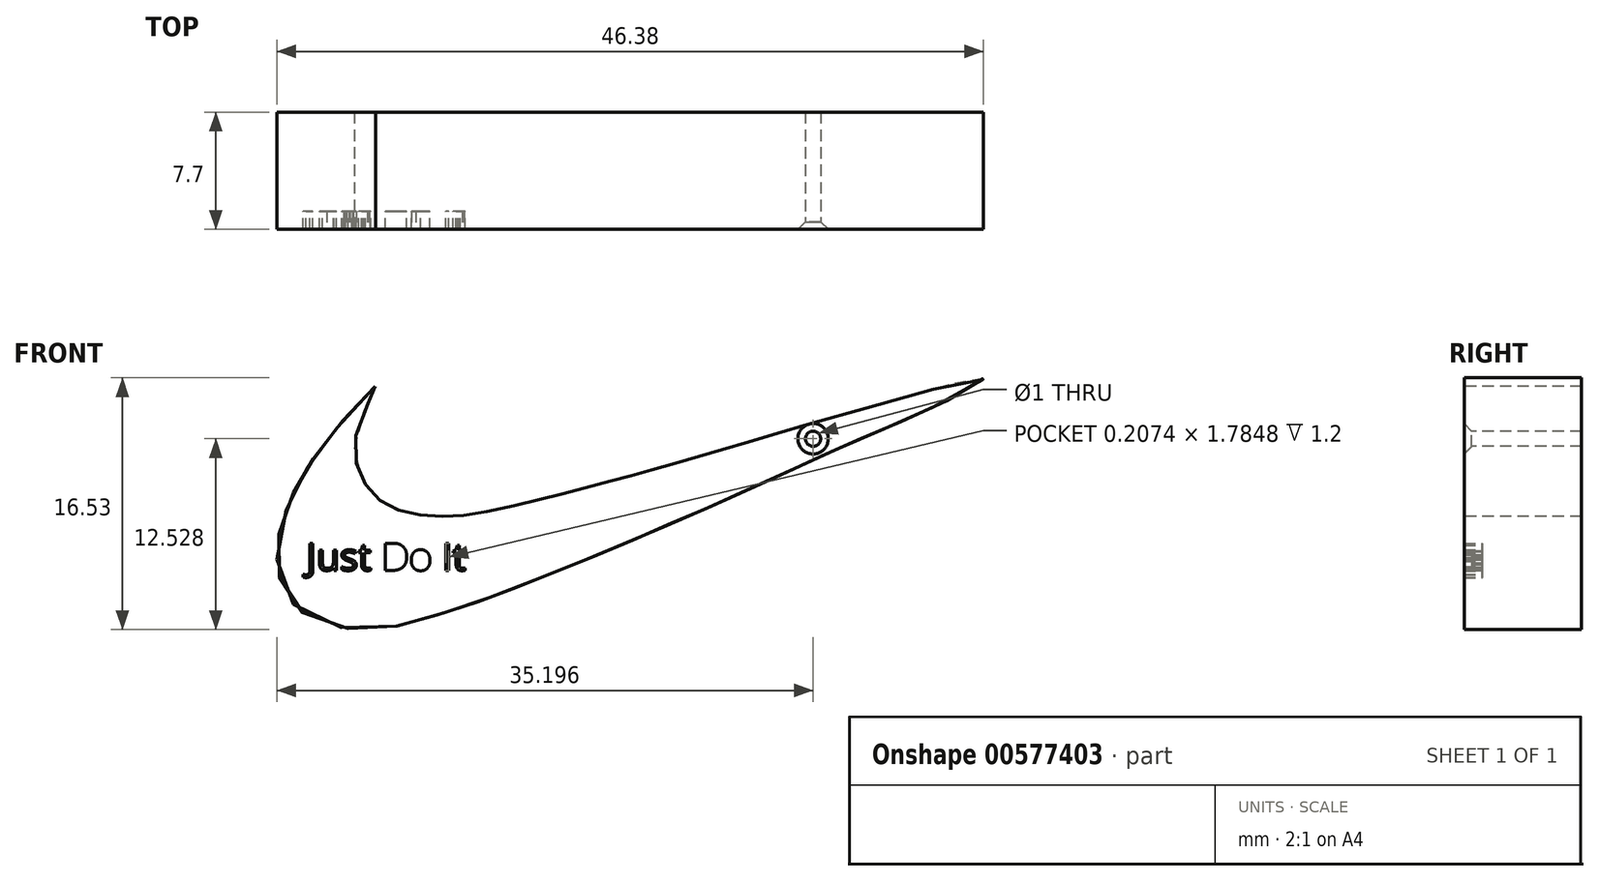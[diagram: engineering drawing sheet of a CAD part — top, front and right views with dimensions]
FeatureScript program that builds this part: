
annotation { "Feature Type Name" : "Feature", "Feature Type Description" : "" }
export const myFeature = defineFeature(function(context is Context, id is Id, definition is map)
    precondition{}
    {
        {
            var Q0;
            Q0=qCreatedBy(makeId("Front.planeOp"),FACE);
            var sketch = newSketch(context, id + "F0", { "sketchPlane" : qUnion([Q0])});
            skFitSpline(sketch, "E0", {"points": [v(-46.77, 38.6) * mm, v(-49.47, 35.68) * mm, v(-51.17, 33.36) * mm, v(-52.4, 31.05) * mm, v(-53.21, 28.05) * mm, v(-52.75, 25.22) * mm, v(-50.6, 23.19) * mm, v(-46.57, 22.67) * mm, v(-43.7, 23.3) * mm, v(-40.92, 24.16) * mm, v(-38.34, 25.09) * mm, v(-35.58, 26.17) * mm, v(-32.72, 27.33) * mm, v(-30.5, 28.24) * mm, v(-28.01, 29.32) * mm, v(-25.64, 30.33) * mm, v(-23.75, 31.18) * mm, v(-21.45, 32.21) * mm, v(-18.28, 33.67) * mm, v(-16.2, 34.6) * mm, v(-13.01, 35.97) * mm, v(-9.7, 37.46) * mm, v(-6.87, 39.13) * mm, v(-11.19, 38.12) * mm, v(-15.96, 36.8) * mm, v(-19.98, 35.64) * mm, v(-23.83, 34.5) * mm, v(-26.45, 33.75) * mm, v(-29.13, 32.98) * mm, v(-31.05, 32.46) * mm, v(-34, 31.67) * mm, v(-36.31, 31.1) * mm, v(-39.68, 30.34) * mm, v(-41.99, 30.07) * mm, v(-44.26, 30.24) * mm, v(-46.26, 30.96) * mm, v(-47.63, 32.56) * mm, v(-47.98, 35.73) * mm, v(-46.77, 38.6) * mm]});
            skSolve(sketch);
        }
        {
            var Q0;
            Q0 = qSketchRegion(id + "F0", true);
            extrude(context, id + "F1", {"entities" : qUnion([Q0]), "depth" : 6.5 * mm, "offsetDistance" : 25 * mm});
        }
        {
            var Q0;
            Q0=makeQuery(id+"F1.opExtrude","CAP_FACE",FACE,{"disambiguationData":[OSD([sQuery(id+"F0.wireOp",EDGE,"E0")])],"isStart":false});
            var sketch = newSketch(context, id + "F2", { "sketchPlane" : qUnion([Q0])});
            skText(sketch, "E1", { "text": "Just Do It", "fontName": "OpenSans-Regular.ttf"});
            const initialGuessF2  = {"E1": [-0.0513, 0.02652, 1, 0, 0.0018]};
            skSetInitialGuess(sketch, initialGuessF2);
            skSolve(sketch);
        }
        {
            var Q0;
            Q0=makeQuery(id+"F2.imprint","IMPRINT",FACE,{"disambiguationData":[TD([[makeQuery(id+"F2.imprint","IMPRINT",EDGE,{"derivedFrom":sQuery(id+"F2.wireOp",EDGE,"E1.sketch_text.stroke-0")}),1.0]])]});
            extrude(context, id + "F3", {"entities" : qUnion([Q0]), "operationType" : NewBodyOperationType.ADD, "depth" : 1.2 * mm, "offsetDistance" : 25 * mm});
        }
        {
            var Q0;
            Q0=makeQuery(id+"F3.opExtrude","CAP_FACE",FACE,{"disambiguationData":[OSD([sQuery(id+"F0.wireOp",EDGE,"E0"),sQuery(id+"F2.wireOp",EDGE,"E1.sketch_text.stroke-0"),sQuery(id+"F2.wireOp",EDGE,"E1.sketch_text.stroke-1"),sQuery(id+"F2.wireOp",EDGE,"E1.sketch_text.stroke-2"),sQuery(id+"F2.wireOp",EDGE,"E1.sketch_text.stroke-3"),sQuery(id+"F2.wireOp",EDGE,"E1.sketch_text.stroke-4"),sQuery(id+"F2.wireOp",EDGE,"E1.sketch_text.stroke-5"),sQuery(id+"F2.wireOp",EDGE,"E1.sketch_text.stroke-6"),sQuery(id+"F2.wireOp",EDGE,"E1.sketch_text.stroke-7"),sQuery(id+"F2.wireOp",EDGE,"E1.sketch_text.stroke-8"),sQuery(id+"F2.wireOp",EDGE,"E1.sketch_text.stroke-9"),sQuery(id+"F2.wireOp",EDGE,"E1.sketch_text.stroke-10"),sQuery(id+"F2.wireOp",EDGE,"E1.sketch_text.stroke-11"),sQuery(id+"F2.wireOp",EDGE,"E1.sketch_text.stroke-12"),sQuery(id+"F2.wireOp",EDGE,"E1.sketch_text.stroke-13"),sQuery(id+"F2.wireOp",EDGE,"E1.sketch_text.stroke-14"),sQuery(id+"F2.wireOp",EDGE,"E1.sketch_text.stroke-15"),sQuery(id+"F2.wireOp",EDGE,"E1.sketch_text.stroke-16"),sQuery(id+"F2.wireOp",EDGE,"E1.sketch_text.stroke-17"),sQuery(id+"F2.wireOp",EDGE,"E1.sketch_text.stroke-18"),sQuery(id+"F2.wireOp",EDGE,"E1.sketch_text.stroke-19"),sQuery(id+"F2.wireOp",EDGE,"E1.sketch_text.stroke-20"),sQuery(id+"F2.wireOp",EDGE,"E1.sketch_text.stroke-21"),sQuery(id+"F2.wireOp",EDGE,"E1.sketch_text.stroke-22"),sQuery(id+"F2.wireOp",EDGE,"E1.sketch_text.stroke-23"),sQuery(id+"F2.wireOp",EDGE,"E1.sketch_text.stroke-24"),sQuery(id+"F2.wireOp",EDGE,"E1.sketch_text.stroke-25"),sQuery(id+"F2.wireOp",EDGE,"E1.sketch_text.stroke-26"),sQuery(id+"F2.wireOp",EDGE,"E1.sketch_text.stroke-27"),sQuery(id+"F2.wireOp",EDGE,"E1.sketch_text.stroke-28"),sQuery(id+"F2.wireOp",EDGE,"E1.sketch_text.stroke-29"),sQuery(id+"F2.wireOp",EDGE,"E1.sketch_text.stroke-30"),sQuery(id+"F2.wireOp",EDGE,"E1.sketch_text.stroke-31"),sQuery(id+"F2.wireOp",EDGE,"E1.sketch_text.stroke-32"),sQuery(id+"F2.wireOp",EDGE,"E1.sketch_text.stroke-33"),sQuery(id+"F2.wireOp",EDGE,"E1.sketch_text.stroke-34"),sQuery(id+"F2.wireOp",EDGE,"E1.sketch_text.stroke-35"),sQuery(id+"F2.wireOp",EDGE,"E1.sketch_text.stroke-36"),sQuery(id+"F2.wireOp",EDGE,"E1.sketch_text.stroke-37"),sQuery(id+"F2.wireOp",EDGE,"E1.sketch_text.stroke-38"),sQuery(id+"F2.wireOp",EDGE,"E1.sketch_text.stroke-39"),sQuery(id+"F2.wireOp",EDGE,"E1.sketch_text.stroke-40"),sQuery(id+"F2.wireOp",EDGE,"E1.sketch_text.stroke-41"),sQuery(id+"F2.wireOp",EDGE,"E1.sketch_text.stroke-42"),sQuery(id+"F2.wireOp",EDGE,"E1.sketch_text.stroke-43"),sQuery(id+"F2.wireOp",EDGE,"E1.sketch_text.stroke-44"),sQuery(id+"F2.wireOp",EDGE,"E1.sketch_text.stroke-45"),sQuery(id+"F2.wireOp",EDGE,"E1.sketch_text.stroke-46"),sQuery(id+"F2.wireOp",EDGE,"E1.sketch_text.stroke-47"),sQuery(id+"F2.wireOp",EDGE,"E1.sketch_text.stroke-48"),sQuery(id+"F2.wireOp",EDGE,"E1.sketch_text.stroke-49"),sQuery(id+"F2.wireOp",EDGE,"E1.sketch_text.stroke-50"),sQuery(id+"F2.wireOp",EDGE,"E1.sketch_text.stroke-51"),sQuery(id+"F2.wireOp",EDGE,"E1.sketch_text.stroke-52"),sQuery(id+"F2.wireOp",EDGE,"E1.sketch_text.stroke-53"),sQuery(id+"F2.wireOp",EDGE,"E1.sketch_text.stroke-54"),sQuery(id+"F2.wireOp",EDGE,"E1.sketch_text.stroke-55"),sQuery(id+"F2.wireOp",EDGE,"E1.sketch_text.stroke-56"),sQuery(id+"F2.wireOp",EDGE,"E1.sketch_text.stroke-57"),sQuery(id+"F2.wireOp",EDGE,"E1.sketch_text.stroke-58"),sQuery(id+"F2.wireOp",EDGE,"E1.sketch_text.stroke-59"),sQuery(id+"F2.wireOp",EDGE,"E1.sketch_text.stroke-60"),sQuery(id+"F2.wireOp",EDGE,"E1.sketch_text.stroke-61"),sQuery(id+"F2.wireOp",EDGE,"E1.sketch_text.stroke-62"),sQuery(id+"F2.wireOp",EDGE,"E1.sketch_text.stroke-63"),sQuery(id+"F2.wireOp",EDGE,"E1.sketch_text.stroke-64"),sQuery(id+"F2.wireOp",EDGE,"E1.sketch_text.stroke-65"),sQuery(id+"F2.wireOp",EDGE,"E1.sketch_text.stroke-66"),sQuery(id+"F2.wireOp",EDGE,"E1.sketch_text.stroke-67"),sQuery(id+"F2.wireOp",EDGE,"E1.sketch_text.stroke-68"),sQuery(id+"F2.wireOp",EDGE,"E1.sketch_text.stroke-69"),sQuery(id+"F2.wireOp",EDGE,"E1.sketch_text.stroke-70"),sQuery(id+"F2.wireOp",EDGE,"E1.sketch_text.stroke-71"),sQuery(id+"F2.wireOp",EDGE,"E1.sketch_text.stroke-72"),sQuery(id+"F2.wireOp",EDGE,"E1.sketch_text.stroke-73"),sQuery(id+"F2.wireOp",EDGE,"E1.sketch_text.stroke-74"),sQuery(id+"F2.wireOp",EDGE,"E1.sketch_text.stroke-75"),sQuery(id+"F2.wireOp",EDGE,"E1.sketch_text.stroke-76"),sQuery(id+"F2.wireOp",EDGE,"E1.sketch_text.stroke-77"),sQuery(id+"F2.wireOp",EDGE,"E1.sketch_text.stroke-85"),sQuery(id+"F2.wireOp",EDGE,"E1.sketch_text.stroke-86"),sQuery(id+"F2.wireOp",EDGE,"E1.sketch_text.stroke-87"),sQuery(id+"F2.wireOp",EDGE,"E1.sketch_text.stroke-88"),sQuery(id+"F2.wireOp",EDGE,"E1.sketch_text.stroke-89"),sQuery(id+"F2.wireOp",EDGE,"E1.sketch_text.stroke-90"),sQuery(id+"F2.wireOp",EDGE,"E1.sketch_text.stroke-91"),sQuery(id+"F2.wireOp",EDGE,"E1.sketch_text.stroke-92"),sQuery(id+"F2.wireOp",EDGE,"E1.sketch_text.stroke-93"),sQuery(id+"F2.wireOp",EDGE,"E1.sketch_text.stroke-102"),sQuery(id+"F2.wireOp",EDGE,"E1.sketch_text.stroke-103"),sQuery(id+"F2.wireOp",EDGE,"E1.sketch_text.stroke-104"),sQuery(id+"F2.wireOp",EDGE,"E1.sketch_text.stroke-105"),sQuery(id+"F2.wireOp",EDGE,"E1.sketch_text.stroke-106"),sQuery(id+"F2.wireOp",EDGE,"E1.sketch_text.stroke-107"),sQuery(id+"F2.wireOp",EDGE,"E1.sketch_text.stroke-108"),sQuery(id+"F2.wireOp",EDGE,"E1.sketch_text.stroke-109"),sQuery(id+"F2.wireOp",EDGE,"E1.sketch_text.stroke-110"),sQuery(id+"F2.wireOp",EDGE,"E1.sketch_text.stroke-111"),sQuery(id+"F2.wireOp",EDGE,"E1.sketch_text.stroke-112"),sQuery(id+"F2.wireOp",EDGE,"E1.sketch_text.stroke-113"),sQuery(id+"F2.wireOp",EDGE,"E1.sketch_text.stroke-114"),sQuery(id+"F2.wireOp",EDGE,"E1.sketch_text.stroke-115"),sQuery(id+"F2.wireOp",EDGE,"E1.sketch_text.stroke-116"),sQuery(id+"F2.wireOp",EDGE,"E1.sketch_text.stroke-117"),sQuery(id+"F2.wireOp",EDGE,"E1.sketch_text.stroke-118"),sQuery(id+"F2.wireOp",EDGE,"E1.sketch_text.stroke-119"),sQuery(id+"F2.wireOp",EDGE,"E1.sketch_text.stroke-120"),sQuery(id+"F2.wireOp",EDGE,"E1.sketch_text.stroke-121"),sQuery(id+"F2.wireOp",EDGE,"E1.sketch_text.stroke-122"),sQuery(id+"F2.wireOp",EDGE,"E1.sketch_text.stroke-123"),sQuery(id+"F2.wireOp",EDGE,"E1.sketch_text.stroke-124")])],"isStart":false});
            var sketch = newSketch(context, id + "F4", { "sketchPlane" : qUnion([Q0])});
            skPoint(sketch, "E2", {"position": v(-18.04, 35.17) * mm});
            skSolve(sketch);
        }
        {
            var Q0;
            Q0=sQuery(id+"F4.wireOp",VERTEX,"E2");
            var Q1;
            Q1=makeQuery(id+"F1.opExtrude","SWEPT_BODY",BODY,{"disambiguationData":[OSD([sQuery(id+"F0.wireOp",EDGE,"E0")])]});
            hole(context, id + "F5", {"style" : HoleStyle.C_SINK, "endStyle" : HoleEndStyle.THROUGH, "holeDiameter" : 1 * mm, "cSinkDiameter" : 2 * mm, "cSinkAngle" : 90 * degree, "majorDiameter" : 5 * mm, "isTappedThrough" : true, "tappedDepth" : 12 * mm, "tapClearance" : 3, "startFromSketch" : true, "locations" : qUnion([Q0]), "scope" : qUnion([Q1])});
        }
    });
